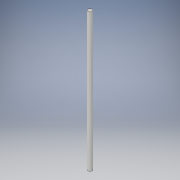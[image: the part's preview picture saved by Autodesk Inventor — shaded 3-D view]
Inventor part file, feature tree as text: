
AUTODESK INVENTOR PART (.ipt)
format: ipt  version: 2019 (Build 230136000, 136)  size: 89,088 bytes
history: native  units: in
note: dims shown in document units (in); Inventor stores cm internally (conversion verified against a paired STEP export)
features: extrude x1, sketch x1
ambient origin geometry x8: Origin, YZ Plane, XZ Plane, XY Plane, X Axis, Y Axis, Z Axis, Center Point
bodies: Solid1 (feature_tree)
feature tree (2):
  extrude  "Extrusion1"  Depth=19.685in TaperAngle=0.0deg
  sketch  "Sketch1"  dims[d0=0.5906in d1=19.685in d2=0.0in]
